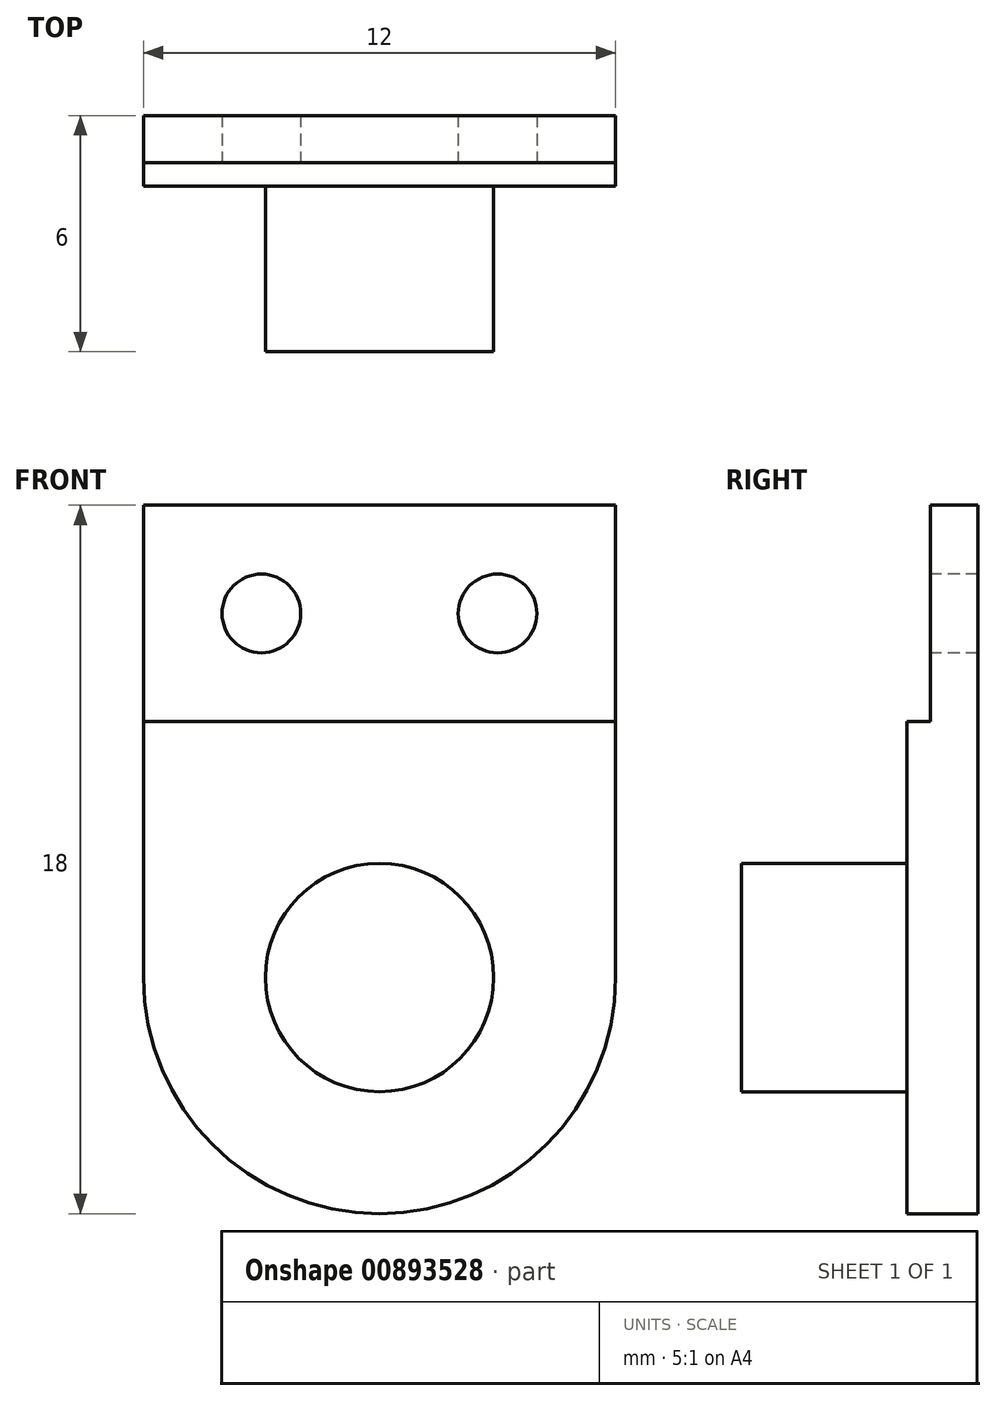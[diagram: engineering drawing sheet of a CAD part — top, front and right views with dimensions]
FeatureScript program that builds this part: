
annotation { "Feature Type Name" : "Feature", "Feature Type Description" : "" }
export const myFeature = defineFeature(function(context is Context, id is Id, definition is map)
    precondition{}
    {
        {
            var Q0;
            Q0=qCreatedBy(makeId("Front.planeOp"),FACE);
            var sketch = newSketch(context, id + "F0", { "sketchPlane" : qUnion([Q0])});
            skLineSegment(sketch, "E0.bottom", {"start": v(6, 9) * mm, "end": v(-6, 9) * mm});
            skLineSegment(sketch, "E0.top", {"start": v(6, -9) * mm, "end": v(-6, -9) * mm});
            skLineSegment(sketch, "E0.left", {"start": v(6, 9) * mm, "end": v(6, -9) * mm});
            skLineSegment(sketch, "E0.right", {"start": v(-6, 9) * mm, "end": v(-6, -9) * mm});
            skPoint(sketch, "E0.middle", {"position": v(0, 0) * mm});
            skSolve(sketch);
        }
        {
            var Q0;
            Q0 = qSketchRegion(id + "F0", true);
            extrude(context, id + "F1", {"entities" : qUnion([Q0]), "depth" : 1.8 * mm, "offsetDistance" : 25 * mm});
        }
        {
            var Q0;
            Q0=makeQuery(id+"F1.opExtrude","SWEPT_EDGE",EDGE,{"disambiguationData":[OSD([sQuery(id+"F0.wireOp",EDGE,"E0.top"),sQuery(id+"F0.wireOp",EDGE,"E0.left")])]});
            var Q1;
            Q1=makeQuery(id+"F1.opExtrude","SWEPT_EDGE",EDGE,{"disambiguationData":[OSD([sQuery(id+"F0.wireOp",EDGE,"E0.top"),sQuery(id+"F0.wireOp",EDGE,"E0.right")])]});
            fillet(context, id + "F2", {"entities" : qUnion([Q0, Q1]), "radius" : 6 * mm, "tangentPropagation" : true, "allowEdgeOverflow" : false});
        }
        {
            var Q0;
            Q0=makeQuery(id+"F1.opExtrude","CAP_FACE",FACE,{"disambiguationData":[OSD([sQuery(id+"F0.wireOp",EDGE,"E0.bottom"),sQuery(id+"F0.wireOp",EDGE,"E0.top"),sQuery(id+"F0.wireOp",EDGE,"E0.left"),sQuery(id+"F0.wireOp",EDGE,"E0.right")])],"isStart":false});
            var sketch = newSketch(context, id + "F3", { "sketchPlane" : qUnion([Q0])});
            skLineSegment(sketch, "E1.bottom", {"start": v(-6, 9) * mm, "end": v(6, 9) * mm});
            skLineSegment(sketch, "E1.top", {"start": v(-6, 3.5) * mm, "end": v(6, 3.5) * mm});
            skLineSegment(sketch, "E1.left", {"start": v(-6, 9) * mm, "end": v(-6, 3.5) * mm});
            skLineSegment(sketch, "E1.right", {"start": v(6, 9) * mm, "end": v(6, 3.5) * mm});
            skSolve(sketch);
        }
        {
            var Q0;
            Q0 = qSketchRegion(id + "F3", true);
            extrude(context, id + "F4", {"entities" : qUnion([Q0]), "operationType" : NewBodyOperationType.REMOVE, "oppositeDirection" : true, "depth" : 0.6 * mm, "offsetDistance" : 25 * mm});
        }
        {
            var Q0;
            Q0=makeQuery(id+"F1.opExtrude","CAP_FACE",FACE,{"disambiguationData":[OSD([sQuery(id+"F0.wireOp",EDGE,"E0.bottom"),sQuery(id+"F0.wireOp",EDGE,"E0.top"),sQuery(id+"F0.wireOp",EDGE,"E0.left"),sQuery(id+"F0.wireOp",EDGE,"E0.right")])],"isStart":false});
            var sketch = newSketch(context, id + "F5", { "sketchPlane" : qUnion([Q0])});
            skCircle(sketch, "E2", {"center": v(0, -3) * mm, "radius": 2.9 * mm});
            skSolve(sketch);
        }
        {
            var Q0;
            Q0 = qSketchRegion(id + "F5", true);
            extrude(context, id + "F6", {"entities" : qUnion([Q0]), "operationType" : NewBodyOperationType.ADD, "depth" : 4.2 * mm, "offsetDistance" : 25 * mm});
        }
        {
            var Q0;
            Q0=makeQuery(id+"F4.boolean.opBoolean","COPY",FACE,{"derivedFrom":makeQuery(id+"F4.opExtrude","CAP_FACE",FACE,{"disambiguationData":[OSD([sQuery(id+"F3.wireOp",EDGE,"E1.bottom"),sQuery(id+"F3.wireOp",EDGE,"E1.top"),sQuery(id+"F3.wireOp",EDGE,"E1.left"),sQuery(id+"F3.wireOp",EDGE,"E1.right")])],"isStart":false})});
            var sketch = newSketch(context, id + "F7", { "sketchPlane" : qUnion([Q0])});
            skLineSegment(sketch, "E3", {"start": v(-6, 6.25) * mm, "end": v(-3, 6.25) * mm, "construction": true});
            skLineSegment(sketch, "E4", {"start": v(-3, 6.25) * mm, "end": v(3, 6.25) * mm, "construction": true});
            skLineSegment(sketch, "E5", {"start": v(3, 6.25) * mm, "end": v(6, 6.25) * mm, "construction": true});
            skCircle(sketch, "E6", {"center": v(-3, 6.25) * mm, "radius": 1 * mm});
            skCircle(sketch, "E7", {"center": v(3, 6.25) * mm, "radius": 1 * mm});
            skSolve(sketch);
        }
        {
            var Q0;
            Q0 = qSketchRegion(id + "F7", true);
            extrude(context, id + "F8", {"entities" : qUnion([Q0]), "operationType" : NewBodyOperationType.REMOVE, "oppositeDirection" : true, "depth" : 25 * mm, "offsetDistance" : 25 * mm});
        }
    });
